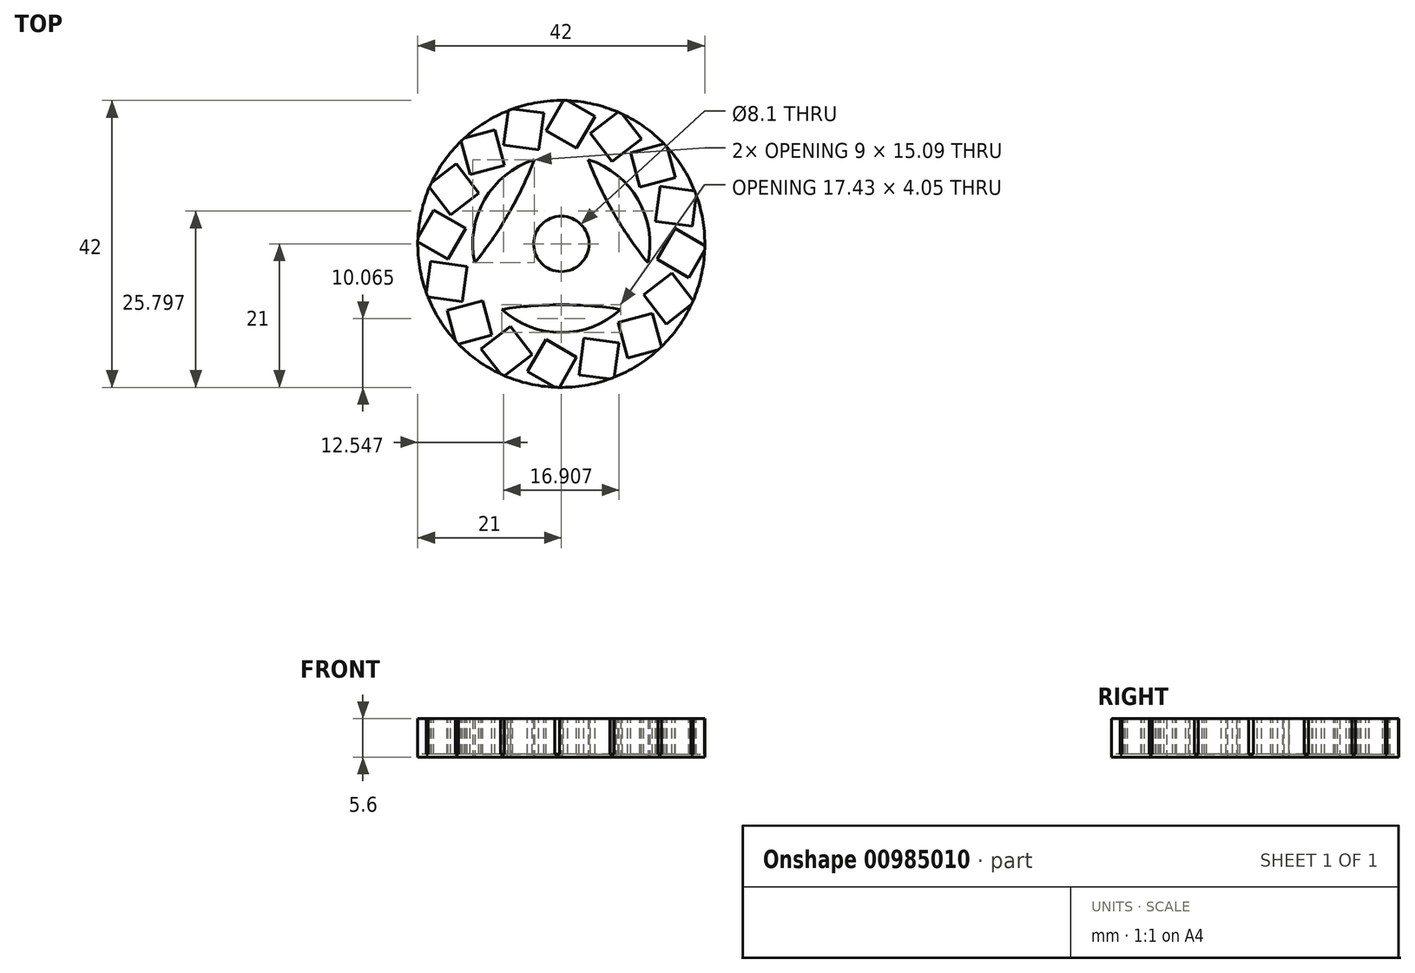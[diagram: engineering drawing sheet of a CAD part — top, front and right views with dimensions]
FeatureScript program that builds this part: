
annotation { "Feature Type Name" : "Feature", "Feature Type Description" : "" }
export const myFeature = defineFeature(function(context is Context, id is Id, definition is map)
    precondition{}
    {
        {
            var Q0;
            Q0=qCreatedBy(makeId("Front.planeOp"),FACE);
            var sketch = newSketch(context, id + "F0", { "sketchPlane" : qUnion([Q0])});
            skLineSegment(sketch, "E0", {"start": v(0, 0) * mm, "end": v(21, 0) * mm});
            skLineSegment(sketch, "E1", {"start": v(21, 0) * mm, "end": v(21, 5.6) * mm});
            skLineSegment(sketch, "E2", {"start": v(21, 5.6) * mm, "end": v(0, 5.6) * mm});
            skLineSegment(sketch, "E3", {"start": v(0, 5.6) * mm, "end": v(0, 0) * mm});
            skSolve(sketch);
        }
        {
            var Q0;
            Q0=qSketchRegion(id+"F0",true);
            var Q1;
            Q1=sQuery(id+"F0.wireOp",EDGE,"E3");
            revolve(context, id + "F1", {"surfaceOperationType" : NewSurfaceOperationType.NEW, "entities" : qUnion([Q0]), "axis" : qUnion([Q1]), "revolveType" : RevolveType.FULL});
        }
        {
            var Q0;
            Q0=qCreatedBy(makeId("Top.planeOp"),FACE);
            var sketch = newSketch(context, id + "F2", { "sketchPlane" : qUnion([Q0])});
            skCircle(sketch, "E4", {"center": v(0, 0) * mm, "radius": 8.9 * mm});
            skCircle(sketch, "E5", {"center": v(0, 0) * mm, "radius": 12.96 * mm});
            skCircle(sketch, "E6", {"center": v(0, 0) * mm, "radius": 17.01 * mm});
            skCircle(sketch, "E7", {"center": v(0, 0) * mm, "radius": 4.05 * mm});
            skCircle(sketch, "E8", {"center": v(0, 12.96) * mm, "radius": 4 * mm});
            skCircle(sketch, "E9.1.0", {"center": v(-11.22, -6.48) * mm, "radius": 4 * mm});
            skCircle(sketch, "E9.2.0", {"center": v(11.22, -6.48) * mm, "radius": 4 * mm});
            skArc(sketch, "E10", {"start": v(-12.67, -2.75) * mm, "mid": v(-7.7, 4.45) * mm, "end": v(-3.95, 12.34) * mm});
            skArc(sketch, "E11", {"start": v(3.95, 12.34) * mm, "mid": v(7.7, 4.44) * mm, "end": v(12.67, -2.75) * mm});
            skArc(sketch, "E12", {"start": v(8.71, -9.6) * mm, "mid": v(0, -8.9) * mm, "end": v(-8.71, -9.6) * mm});
            skLineSegment(sketch, "E13", {"start": v(-3.95, 12.34) * mm, "end": v(-4.58, 16.38) * mm});
            skLineSegment(sketch, "E14", {"start": v(3.95, 12.34) * mm, "end": v(4.58, 16.38) * mm});
            skLineSegment(sketch, "E15.1.0", {"start": v(-8.71, -9.6) * mm, "end": v(-11.9, -12.16) * mm});
            skLineSegment(sketch, "E15.1.1", {"start": v(-12.67, -2.75) * mm, "end": v(-16.48, -4.22) * mm});
            skLineSegment(sketch, "E15.2.0", {"start": v(12.67, -2.75) * mm, "end": v(16.48, -4.22) * mm});
            skLineSegment(sketch, "E15.2.1", {"start": v(8.71, -9.6) * mm, "end": v(11.9, -12.16) * mm});
            skSolve(sketch);
        }
        {
            var Q0;
            Q0=makeQuery(id+"F2.imprint","IMPRINT",FACE,{"disambiguationData":[TD([[makeQuery(id+"F2.imprint","IMPRINT",EDGE,{"derivedFrom":sQuery(id+"F2.wireOp",EDGE,"E7")}),1.0]])]});
            var Q1;
            {var subQ0=sQuery(id+"F2.wireOp",EDGE,"E10");var subQ1=sQuery(id+"F2.wireOp",EDGE,"E4");var subQ2=makeQuery(id+"F2.imprint","INTERSECT",VERTEX,{"disambiguationData":[OD(0.0)],"derivedFrom":[subQ1,subQ0]});Q1=makeQuery(id+"F2.imprint","IMPRINT",FACE,{"disambiguationData":[TD([[makeQuery(id+"F2.imprint","IMPRINT",EDGE,{"disambiguationData":[TD([[subQ2,-1.0]])],"derivedFrom":subQ1}),-1.0]])]});}
            var Q2;
            {var subQ0=sQuery(id+"F2.wireOp",EDGE,"E11");var subQ1=sQuery(id+"F2.wireOp",EDGE,"E4");var subQ2=makeQuery(id+"F2.imprint","INTERSECT",VERTEX,{"disambiguationData":[OD(0.0)],"derivedFrom":[subQ1,subQ0]});Q2=makeQuery(id+"F2.imprint","IMPRINT",FACE,{"disambiguationData":[TD([[makeQuery(id+"F2.imprint","IMPRINT",EDGE,{"disambiguationData":[TD([[subQ2,1.0]])],"derivedFrom":subQ1}),-1.0]])]});}
            var Q3;
            {var subQ0=sQuery(id+"F2.wireOp",EDGE,"E12");var subQ1=sQuery(id+"F2.wireOp",EDGE,"E4");var subQ2=makeQuery(id+"F2.imprint","INTERSECT",VERTEX,{"disambiguationData":[OD(0.0)],"derivedFrom":[subQ1,subQ0]});Q3=makeQuery(id+"F2.imprint","IMPRINT",FACE,{"disambiguationData":[TD([[makeQuery(id+"F2.imprint","IMPRINT",EDGE,{"disambiguationData":[TD([[subQ2,-1.0]])],"derivedFrom":subQ1}),-1.0]])]});}
            extrude(context, id + "F3", {"entities" : qUnion([Q0, Q1, Q2, Q3]), "operationType" : NewBodyOperationType.REMOVE, "depth" : 25 * mm, "offsetDistance" : 25 * mm});
        }
        {
            var Q0;
            Q0=makeQuery(id+"F1.opRevolve","SWEPT_FACE",FACE,{"disambiguationData":[OSD([sQuery(id+"F0.wireOp",EDGE,"E2")])]});
            var sketch = newSketch(context, id + "F4", { "sketchPlane" : qUnion([Q0])});
            skLineSegment(sketch, "E16.bottom", {"start": v(2.25, 14) * mm, "end": v(-2.25, 16.6) * mm});
            skLineSegment(sketch, "E16.top", {"start": v(4.95, 18.68) * mm, "end": v(0.45, 21.28) * mm});
            skLineSegment(sketch, "E16.left", {"start": v(2.25, 14) * mm, "end": v(4.95, 18.68) * mm});
            skLineSegment(sketch, "E16.right", {"start": v(-2.25, 16.6) * mm, "end": v(0.45, 21.28) * mm});
            skLineSegment(sketch, "E17", {"start": v(0, 0) * mm, "end": v(0, 15.3) * mm, "construction": true});
            skLineSegment(sketch, "E18.1.0", {"start": v(-3.28, 13.8) * mm, "end": v(-2.57, 19.15) * mm});
            skLineSegment(sketch, "E18.1.1", {"start": v(-2.57, 19.15) * mm, "end": v(-7.73, 19.83) * mm});
            skLineSegment(sketch, "E18.1.2", {"start": v(-8.43, 14.47) * mm, "end": v(-7.73, 19.83) * mm});
            skLineSegment(sketch, "E18.1.3", {"start": v(-3.28, 13.8) * mm, "end": v(-8.43, 14.47) * mm});
            skLineSegment(sketch, "E18.2.0", {"start": v(-8.3, 11.5) * mm, "end": v(-9.7, 16.7) * mm});
            skLineSegment(sketch, "E18.2.1", {"start": v(-9.7, 16.7) * mm, "end": v(-14.73, 15.36) * mm});
            skLineSegment(sketch, "E18.2.2", {"start": v(-13.33, 10.15) * mm, "end": v(-14.73, 15.36) * mm});
            skLineSegment(sketch, "E18.2.3", {"start": v(-8.3, 11.5) * mm, "end": v(-13.33, 10.15) * mm});
            skLineSegment(sketch, "E18.3.0", {"start": v(-12.07, 7.44) * mm, "end": v(-15.36, 11.72) * mm});
            skLineSegment(sketch, "E18.3.1", {"start": v(-15.36, 11.72) * mm, "end": v(-19.49, 8.56) * mm});
            skLineSegment(sketch, "E18.3.2", {"start": v(-16.2, 4.27) * mm, "end": v(-19.49, 8.56) * mm});
            skLineSegment(sketch, "E18.3.3", {"start": v(-12.07, 7.44) * mm, "end": v(-16.2, 4.27) * mm});
            skLineSegment(sketch, "E18.4.0", {"start": v(-14, 2.25) * mm, "end": v(-18.68, 4.95) * mm});
            skLineSegment(sketch, "E18.4.1", {"start": v(-18.68, 4.95) * mm, "end": v(-21.28, 0.45) * mm});
            skLineSegment(sketch, "E18.4.2", {"start": v(-16.6, -2.25) * mm, "end": v(-21.28, 0.45) * mm});
            skLineSegment(sketch, "E18.4.3", {"start": v(-14, 2.25) * mm, "end": v(-16.6, -2.25) * mm});
            skLineSegment(sketch, "E18.5.0", {"start": v(-13.8, -3.28) * mm, "end": v(-19.15, -2.57) * mm});
            skLineSegment(sketch, "E18.5.1", {"start": v(-19.15, -2.57) * mm, "end": v(-19.83, -7.73) * mm});
            skLineSegment(sketch, "E18.5.2", {"start": v(-14.47, -8.43) * mm, "end": v(-19.83, -7.73) * mm});
            skLineSegment(sketch, "E18.5.3", {"start": v(-13.8, -3.28) * mm, "end": v(-14.47, -8.43) * mm});
            skLineSegment(sketch, "E18.6.0", {"start": v(-11.5, -8.3) * mm, "end": v(-16.7, -9.7) * mm});
            skLineSegment(sketch, "E18.6.1", {"start": v(-16.7, -9.7) * mm, "end": v(-15.36, -14.73) * mm});
            skLineSegment(sketch, "E18.6.2", {"start": v(-10.15, -13.33) * mm, "end": v(-15.36, -14.73) * mm});
            skLineSegment(sketch, "E18.6.3", {"start": v(-11.5, -8.3) * mm, "end": v(-10.15, -13.33) * mm});
            skLineSegment(sketch, "E18.7.0", {"start": v(-7.44, -12.07) * mm, "end": v(-11.72, -15.36) * mm});
            skLineSegment(sketch, "E18.7.1", {"start": v(-11.72, -15.36) * mm, "end": v(-8.56, -19.49) * mm});
            skLineSegment(sketch, "E18.7.2", {"start": v(-4.27, -16.2) * mm, "end": v(-8.56, -19.49) * mm});
            skLineSegment(sketch, "E18.7.3", {"start": v(-7.44, -12.07) * mm, "end": v(-4.27, -16.2) * mm});
            skLineSegment(sketch, "E18.8.0", {"start": v(-2.25, -14) * mm, "end": v(-4.95, -18.68) * mm});
            skLineSegment(sketch, "E18.8.1", {"start": v(-4.95, -18.68) * mm, "end": v(-0.45, -21.28) * mm});
            skLineSegment(sketch, "E18.8.2", {"start": v(2.25, -16.6) * mm, "end": v(-0.45, -21.28) * mm});
            skLineSegment(sketch, "E18.8.3", {"start": v(-2.25, -14) * mm, "end": v(2.25, -16.6) * mm});
            skLineSegment(sketch, "E18.9.0", {"start": v(3.28, -13.8) * mm, "end": v(2.57, -19.15) * mm});
            skLineSegment(sketch, "E18.9.1", {"start": v(2.57, -19.15) * mm, "end": v(7.73, -19.83) * mm});
            skLineSegment(sketch, "E18.9.2", {"start": v(8.43, -14.47) * mm, "end": v(7.73, -19.83) * mm});
            skLineSegment(sketch, "E18.9.3", {"start": v(3.28, -13.8) * mm, "end": v(8.43, -14.47) * mm});
            skLineSegment(sketch, "E18.10.0", {"start": v(8.3, -11.5) * mm, "end": v(9.7, -16.7) * mm});
            skLineSegment(sketch, "E18.10.1", {"start": v(9.7, -16.7) * mm, "end": v(14.73, -15.36) * mm});
            skLineSegment(sketch, "E18.10.2", {"start": v(13.33, -10.15) * mm, "end": v(14.73, -15.36) * mm});
            skLineSegment(sketch, "E18.10.3", {"start": v(8.3, -11.5) * mm, "end": v(13.33, -10.15) * mm});
            skLineSegment(sketch, "E18.11.0", {"start": v(12.07, -7.44) * mm, "end": v(15.36, -11.72) * mm});
            skLineSegment(sketch, "E18.11.1", {"start": v(15.36, -11.72) * mm, "end": v(19.49, -8.56) * mm});
            skLineSegment(sketch, "E18.11.2", {"start": v(16.2, -4.27) * mm, "end": v(19.49, -8.56) * mm});
            skLineSegment(sketch, "E18.11.3", {"start": v(12.07, -7.44) * mm, "end": v(16.2, -4.27) * mm});
            skLineSegment(sketch, "E18.12.0", {"start": v(14, -2.25) * mm, "end": v(18.68, -4.95) * mm});
            skLineSegment(sketch, "E18.12.1", {"start": v(18.68, -4.95) * mm, "end": v(21.28, -0.45) * mm});
            skLineSegment(sketch, "E18.12.2", {"start": v(16.6, 2.25) * mm, "end": v(21.28, -0.45) * mm});
            skLineSegment(sketch, "E18.12.3", {"start": v(14, -2.25) * mm, "end": v(16.6, 2.25) * mm});
            skLineSegment(sketch, "E18.13.0", {"start": v(13.8, 3.28) * mm, "end": v(19.15, 2.57) * mm});
            skLineSegment(sketch, "E18.13.1", {"start": v(19.15, 2.57) * mm, "end": v(19.83, 7.73) * mm});
            skLineSegment(sketch, "E18.13.2", {"start": v(14.47, 8.43) * mm, "end": v(19.83, 7.73) * mm});
            skLineSegment(sketch, "E18.13.3", {"start": v(13.8, 3.28) * mm, "end": v(14.47, 8.43) * mm});
            skLineSegment(sketch, "E18.14.0", {"start": v(11.5, 8.3) * mm, "end": v(16.7, 9.7) * mm});
            skLineSegment(sketch, "E18.14.1", {"start": v(16.7, 9.7) * mm, "end": v(15.36, 14.73) * mm});
            skLineSegment(sketch, "E18.14.2", {"start": v(10.15, 13.33) * mm, "end": v(15.36, 14.73) * mm});
            skLineSegment(sketch, "E18.14.3", {"start": v(11.5, 8.3) * mm, "end": v(10.15, 13.33) * mm});
            skLineSegment(sketch, "E18.15.0", {"start": v(7.44, 12.07) * mm, "end": v(11.72, 15.36) * mm});
            skLineSegment(sketch, "E18.15.1", {"start": v(11.72, 15.36) * mm, "end": v(8.56, 19.49) * mm});
            skLineSegment(sketch, "E18.15.2", {"start": v(4.27, 16.2) * mm, "end": v(8.56, 19.49) * mm});
            skLineSegment(sketch, "E18.15.3", {"start": v(7.44, 12.07) * mm, "end": v(4.27, 16.2) * mm});
            skPoint(sketch, "E18.center", {"position": v(0, 0) * mm});
            skLineSegment(sketch, "E19", {"start": v(0, 0) * mm, "end": v(0, 21) * mm});
            skLineSegment(sketch, "E20.1.0", {"start": v(0, 0) * mm, "end": v(-18.19, -10.5) * mm});
            skLineSegment(sketch, "E20.2.0", {"start": v(0, 0) * mm, "end": v(18.19, -10.5) * mm});
            skLineSegment(sketch, "E21", {"start": v(0, 15.3) * mm, "end": v(0, 15.7) * mm});
            skSolve(sketch);
        }
        {
            var Q0;
            {var subQ0=sQuery(id+"F4.wireOp",EDGE,"6b0e4d02-cffa-4799-8ca5-8f1609af44a9.1.3");Q0=makeQuery(id+"F4.imprint","IMPRINT",FACE,{"disambiguationData":[TD([[makeQuery(id+"F4.imprint","IMPRINT",EDGE,{"derivedFrom":subQ0}),-1.0]])]});}
            var Q1;
            {var subQ0=sQuery(id+"F4.wireOp",EDGE,"E16.bottom");Q1=makeQuery(id+"F4.imprint","IMPRINT",FACE,{"disambiguationData":[TD([[makeQuery(id+"F4.imprint","IMPRINT",EDGE,{"derivedFrom":subQ0}),-1.0]])]});}
            var Q2;
            {var subQ0=sQuery(id+"F4.wireOp",EDGE,"90cd43ab-74c5-4661-9c80-5ee8405ae9ff.9.15.0");Q2=makeQuery(id+"F4.imprint","IMPRINT",FACE,{"disambiguationData":[TD([[makeQuery(id+"F4.imprint","IMPRINT",EDGE,{"derivedFrom":subQ0}),-1.0]])]});}
            var Q3;
            {var subQ0=sQuery(id+"F4.wireOp",EDGE,"90cd43ab-74c5-4661-9c80-5ee8405ae9ff.9.14.0");Q3=makeQuery(id+"F4.imprint","IMPRINT",FACE,{"disambiguationData":[TD([[makeQuery(id+"F4.imprint","IMPRINT",EDGE,{"derivedFrom":subQ0}),-1.0]])]});}
            var Q4;
            {var subQ0=sQuery(id+"F4.wireOp",EDGE,"90cd43ab-74c5-4661-9c80-5ee8405ae9ff.9.13.0");Q4=makeQuery(id+"F4.imprint","IMPRINT",FACE,{"disambiguationData":[TD([[makeQuery(id+"F4.imprint","IMPRINT",EDGE,{"derivedFrom":subQ0}),-1.0]])]});}
            var Q5;
            {var subQ0=sQuery(id+"F4.wireOp",EDGE,"90cd43ab-74c5-4661-9c80-5ee8405ae9ff.9.12.0");Q5=makeQuery(id+"F4.imprint","IMPRINT",FACE,{"disambiguationData":[TD([[makeQuery(id+"F4.imprint","IMPRINT",EDGE,{"derivedFrom":subQ0}),-1.0]])]});}
            var Q6;
            {var subQ0=sQuery(id+"F4.wireOp",EDGE,"90cd43ab-74c5-4661-9c80-5ee8405ae9ff.9.11.0");Q6=makeQuery(id+"F4.imprint","IMPRINT",FACE,{"disambiguationData":[TD([[makeQuery(id+"F4.imprint","IMPRINT",EDGE,{"derivedFrom":subQ0}),-1.0]])]});}
            var Q7;
            {var subQ0=sQuery(id+"F4.wireOp",EDGE,"90cd43ab-74c5-4661-9c80-5ee8405ae9ff.9.10.0");Q7=makeQuery(id+"F4.imprint","IMPRINT",FACE,{"disambiguationData":[TD([[makeQuery(id+"F4.imprint","IMPRINT",EDGE,{"derivedFrom":subQ0}),-1.0]])]});}
            var Q8;
            {var subQ0=sQuery(id+"F4.wireOp",EDGE,"90cd43ab-74c5-4661-9c80-5ee8405ae9ff.9.9.0");Q8=makeQuery(id+"F4.imprint","IMPRINT",FACE,{"disambiguationData":[TD([[makeQuery(id+"F4.imprint","IMPRINT",EDGE,{"derivedFrom":subQ0}),-1.0]])]});}
            var Q9;
            {var subQ0=sQuery(id+"F4.wireOp",EDGE,"90cd43ab-74c5-4661-9c80-5ee8405ae9ff.9.8.0");Q9=makeQuery(id+"F4.imprint","IMPRINT",FACE,{"disambiguationData":[TD([[makeQuery(id+"F4.imprint","IMPRINT",EDGE,{"derivedFrom":subQ0}),-1.0]])]});}
            var Q10;
            {var subQ0=sQuery(id+"F4.wireOp",EDGE,"90cd43ab-74c5-4661-9c80-5ee8405ae9ff.9.7.0");Q10=makeQuery(id+"F4.imprint","IMPRINT",FACE,{"disambiguationData":[TD([[makeQuery(id+"F4.imprint","IMPRINT",EDGE,{"derivedFrom":subQ0}),-1.0]])]});}
            var Q11;
            {var subQ0=sQuery(id+"F4.wireOp",EDGE,"90cd43ab-74c5-4661-9c80-5ee8405ae9ff.9.6.0");Q11=makeQuery(id+"F4.imprint","IMPRINT",FACE,{"disambiguationData":[TD([[makeQuery(id+"F4.imprint","IMPRINT",EDGE,{"derivedFrom":subQ0}),-1.0]])]});}
            var Q12;
            {var subQ0=sQuery(id+"F4.wireOp",EDGE,"90cd43ab-74c5-4661-9c80-5ee8405ae9ff.9.5.0");Q12=makeQuery(id+"F4.imprint","IMPRINT",FACE,{"disambiguationData":[TD([[makeQuery(id+"F4.imprint","IMPRINT",EDGE,{"derivedFrom":subQ0}),-1.0]])]});}
            var Q13;
            {var subQ0=sQuery(id+"F4.wireOp",EDGE,"90cd43ab-74c5-4661-9c80-5ee8405ae9ff.9.4.0");Q13=makeQuery(id+"F4.imprint","IMPRINT",FACE,{"disambiguationData":[TD([[makeQuery(id+"F4.imprint","IMPRINT",EDGE,{"derivedFrom":subQ0}),-1.0]])]});}
            var Q14;
            {var subQ0=sQuery(id+"F4.wireOp",EDGE,"90cd43ab-74c5-4661-9c80-5ee8405ae9ff.9.3.0");Q14=makeQuery(id+"F4.imprint","IMPRINT",FACE,{"disambiguationData":[TD([[makeQuery(id+"F4.imprint","IMPRINT",EDGE,{"derivedFrom":subQ0}),-1.0]])]});}
            var Q15;
            {var subQ0=sQuery(id+"F4.wireOp",EDGE,"6b0e4d02-cffa-4799-8ca5-8f1609af44a9.2.3");Q15=makeQuery(id+"F4.imprint","IMPRINT",FACE,{"disambiguationData":[TD([[makeQuery(id+"F4.imprint","IMPRINT",EDGE,{"derivedFrom":subQ0}),-1.0]])]});}
            var Q16;
            Q16=makeQuery(id+"F4.imprint","IMPRINT",FACE,{"disambiguationData":[TD([[makeQuery(id+"F4.imprint","IMPRINT",EDGE,{"derivedFrom":sQuery(id+"F4.wireOp",EDGE,"d7aad85c-847f-47a7-b33a-bcce6dfe605d.15.0")}),-1.0]])]});
            var Q17;
            Q17=makeQuery(id+"F4.imprint","IMPRINT",FACE,{"disambiguationData":[TD([[makeQuery(id+"F4.imprint","IMPRINT",EDGE,{"derivedFrom":sQuery(id+"F4.wireOp",EDGE,"d7aad85c-847f-47a7-b33a-bcce6dfe605d.14.0")}),-1.0]])]});
            var Q18;
            Q18=makeQuery(id+"F4.imprint","IMPRINT",FACE,{"disambiguationData":[TD([[makeQuery(id+"F4.imprint","IMPRINT",EDGE,{"derivedFrom":sQuery(id+"F4.wireOp",EDGE,"d7aad85c-847f-47a7-b33a-bcce6dfe605d.13.0")}),-1.0]])]});
            var Q19;
            Q19=makeQuery(id+"F4.imprint","IMPRINT",FACE,{"disambiguationData":[TD([[makeQuery(id+"F4.imprint","IMPRINT",EDGE,{"derivedFrom":sQuery(id+"F4.wireOp",EDGE,"d7aad85c-847f-47a7-b33a-bcce6dfe605d.12.0")}),-1.0]])]});
            var Q20;
            Q20=makeQuery(id+"F4.imprint","IMPRINT",FACE,{"disambiguationData":[TD([[makeQuery(id+"F4.imprint","IMPRINT",EDGE,{"derivedFrom":sQuery(id+"F4.wireOp",EDGE,"d7aad85c-847f-47a7-b33a-bcce6dfe605d.11.0")}),-1.0]])]});
            var Q21;
            Q21=makeQuery(id+"F4.imprint","IMPRINT",FACE,{"disambiguationData":[TD([[makeQuery(id+"F4.imprint","IMPRINT",EDGE,{"derivedFrom":sQuery(id+"F4.wireOp",EDGE,"d7aad85c-847f-47a7-b33a-bcce6dfe605d.10.0")}),-1.0]])]});
            var Q22;
            Q22=makeQuery(id+"F4.imprint","IMPRINT",FACE,{"disambiguationData":[TD([[makeQuery(id+"F4.imprint","IMPRINT",EDGE,{"derivedFrom":sQuery(id+"F4.wireOp",EDGE,"d7aad85c-847f-47a7-b33a-bcce6dfe605d.9.0")}),-1.0]])]});
            var Q23;
            Q23=makeQuery(id+"F4.imprint","IMPRINT",FACE,{"disambiguationData":[TD([[makeQuery(id+"F4.imprint","IMPRINT",EDGE,{"derivedFrom":sQuery(id+"F4.wireOp",EDGE,"d7aad85c-847f-47a7-b33a-bcce6dfe605d.8.0")}),-1.0]])]});
            var Q24;
            Q24=makeQuery(id+"F4.imprint","IMPRINT",FACE,{"disambiguationData":[TD([[makeQuery(id+"F4.imprint","IMPRINT",EDGE,{"derivedFrom":sQuery(id+"F4.wireOp",EDGE,"d7aad85c-847f-47a7-b33a-bcce6dfe605d.7.0")}),-1.0]])]});
            var Q25;
            Q25=makeQuery(id+"F4.imprint","IMPRINT",FACE,{"disambiguationData":[TD([[makeQuery(id+"F4.imprint","IMPRINT",EDGE,{"derivedFrom":sQuery(id+"F4.wireOp",EDGE,"d7aad85c-847f-47a7-b33a-bcce6dfe605d.6.0")}),-1.0]])]});
            var Q26;
            Q26=makeQuery(id+"F4.imprint","IMPRINT",FACE,{"disambiguationData":[TD([[makeQuery(id+"F4.imprint","IMPRINT",EDGE,{"derivedFrom":sQuery(id+"F4.wireOp",EDGE,"d7aad85c-847f-47a7-b33a-bcce6dfe605d.5.0")}),-1.0]])]});
            var Q27;
            Q27=makeQuery(id+"F4.imprint","IMPRINT",FACE,{"disambiguationData":[TD([[makeQuery(id+"F4.imprint","IMPRINT",EDGE,{"derivedFrom":sQuery(id+"F4.wireOp",EDGE,"d7aad85c-847f-47a7-b33a-bcce6dfe605d.4.0")}),-1.0]])]});
            var Q28;
            Q28=makeQuery(id+"F4.imprint","IMPRINT",FACE,{"disambiguationData":[TD([[makeQuery(id+"F4.imprint","IMPRINT",EDGE,{"derivedFrom":sQuery(id+"F4.wireOp",EDGE,"d7aad85c-847f-47a7-b33a-bcce6dfe605d.3.0")}),-1.0]])]});
            var Q29;
            Q29=makeQuery(id+"F4.imprint","IMPRINT",FACE,{"disambiguationData":[TD([[makeQuery(id+"F4.imprint","IMPRINT",EDGE,{"derivedFrom":sQuery(id+"F4.wireOp",EDGE,"d7aad85c-847f-47a7-b33a-bcce6dfe605d.2.0")}),-1.0]])]});
            var Q30;
            Q30=makeQuery(id+"F4.imprint","IMPRINT",FACE,{"disambiguationData":[TD([[makeQuery(id+"F4.imprint","IMPRINT",EDGE,{"derivedFrom":sQuery(id+"F4.wireOp",EDGE,"d7aad85c-847f-47a7-b33a-bcce6dfe605d.1.0")}),-1.0]])]});
            var Q31;
            Q31=makeQuery(id+"F4.imprint","IMPRINT",FACE,{"disambiguationData":[TD([[makeQuery(id+"F4.imprint","IMPRINT",EDGE,{"derivedFrom":sQuery(id+"F4.wireOp",EDGE,"E18.15.0")}),1.0]])]});
            var Q32;
            Q32=makeQuery(id+"F4.imprint","IMPRINT",FACE,{"disambiguationData":[TD([[makeQuery(id+"F4.imprint","IMPRINT",EDGE,{"derivedFrom":sQuery(id+"F4.wireOp",EDGE,"E18.14.0")}),1.0]])]});
            var Q33;
            Q33=makeQuery(id+"F4.imprint","IMPRINT",FACE,{"disambiguationData":[TD([[makeQuery(id+"F4.imprint","IMPRINT",EDGE,{"derivedFrom":sQuery(id+"F4.wireOp",EDGE,"E18.13.0")}),1.0]])]});
            var Q34;
            Q34=makeQuery(id+"F4.imprint","IMPRINT",FACE,{"disambiguationData":[TD([[makeQuery(id+"F4.imprint","IMPRINT",EDGE,{"derivedFrom":sQuery(id+"F4.wireOp",EDGE,"E18.12.0")}),1.0]])]});
            var Q35;
            Q35=makeQuery(id+"F4.imprint","IMPRINT",FACE,{"disambiguationData":[TD([[makeQuery(id+"F4.imprint","IMPRINT",EDGE,{"derivedFrom":sQuery(id+"F4.wireOp",EDGE,"E18.11.0")}),1.0]])]});
            var Q36;
            Q36=makeQuery(id+"F4.imprint","IMPRINT",FACE,{"disambiguationData":[TD([[makeQuery(id+"F4.imprint","IMPRINT",EDGE,{"derivedFrom":sQuery(id+"F4.wireOp",EDGE,"E18.10.0")}),1.0]])]});
            var Q37;
            Q37=makeQuery(id+"F4.imprint","IMPRINT",FACE,{"disambiguationData":[TD([[makeQuery(id+"F4.imprint","IMPRINT",EDGE,{"derivedFrom":sQuery(id+"F4.wireOp",EDGE,"E18.9.0")}),1.0]])]});
            var Q38;
            Q38=makeQuery(id+"F4.imprint","IMPRINT",FACE,{"disambiguationData":[TD([[makeQuery(id+"F4.imprint","IMPRINT",EDGE,{"derivedFrom":sQuery(id+"F4.wireOp",EDGE,"E18.8.0")}),1.0]])]});
            var Q39;
            Q39=makeQuery(id+"F4.imprint","IMPRINT",FACE,{"disambiguationData":[TD([[makeQuery(id+"F4.imprint","IMPRINT",EDGE,{"derivedFrom":sQuery(id+"F4.wireOp",EDGE,"E18.7.0")}),1.0]])]});
            var Q40;
            Q40=makeQuery(id+"F4.imprint","IMPRINT",FACE,{"disambiguationData":[TD([[makeQuery(id+"F4.imprint","IMPRINT",EDGE,{"derivedFrom":sQuery(id+"F4.wireOp",EDGE,"E18.6.0")}),1.0]])]});
            var Q41;
            Q41=makeQuery(id+"F4.imprint","IMPRINT",FACE,{"disambiguationData":[TD([[makeQuery(id+"F4.imprint","IMPRINT",EDGE,{"derivedFrom":sQuery(id+"F4.wireOp",EDGE,"E18.4.0")}),1.0]])]});
            var Q42;
            Q42=makeQuery(id+"F4.imprint","IMPRINT",FACE,{"disambiguationData":[TD([[makeQuery(id+"F4.imprint","IMPRINT",EDGE,{"derivedFrom":sQuery(id+"F4.wireOp",EDGE,"E18.3.0")}),1.0]])]});
            var Q43;
            Q43=makeQuery(id+"F4.imprint","IMPRINT",FACE,{"disambiguationData":[TD([[makeQuery(id+"F4.imprint","IMPRINT",EDGE,{"derivedFrom":sQuery(id+"F4.wireOp",EDGE,"E18.2.0")}),1.0]])]});
            var Q44;
            Q44=makeQuery(id+"F4.imprint","IMPRINT",FACE,{"disambiguationData":[TD([[makeQuery(id+"F4.imprint","IMPRINT",EDGE,{"derivedFrom":sQuery(id+"F4.wireOp",EDGE,"E18.1.0")}),1.0]])]});
            var Q45;
            {var subQ0=sQuery(id+"F4.wireOp",EDGE,"E18.5.0");var subQ1=sQuery(id+"F2.wireOp",EDGE,"E15.1.1");var subQ2=makeQuery(id+"F1.opRevolve","SWEPT_FACE",FACE,{"disambiguationData":[OSD([sQuery(id+"F0.wireOp",EDGE,"E2")])]});var subQ3=makeQuery(id+"F3.boolean.opBoolean","INTERSECT",EDGE,{"derivedFrom":[subQ2,makeQuery(id+"F3.opExtrude","SWEPT_FACE",FACE,{"disambiguationData":[OSD([subQ1])]})]});var subQ4=makeQuery(id+"F4.imprint","INTERSECT",VERTEX,{"derivedFrom":[subQ3,subQ0]});Q45=makeQuery(id+"F4.imprint","IMPRINT",FACE,{"disambiguationData":[TD([[makeQuery(id+"F4.imprint","IMPRINT",EDGE,{"disambiguationData":[TD([[subQ4,-1.0]])],"derivedFrom":subQ0}),1.0]])]});}
            var Q46;
            {var subQ0=sQuery(id+"F4.wireOp",EDGE,"E18.1.3");var subQ1=sQuery(id+"F4.wireOp",EDGE,"E18.1.2");var subQ2=makeQuery(id+"F4.imprint","INTERSECT",VERTEX,{"derivedFrom":[subQ1,subQ0]});Q46=makeQuery(id+"F4.imprint","IMPRINT",FACE,{"disambiguationData":[TD([[makeQuery(id+"F4.imprint","IMPRINT",EDGE,{"disambiguationData":[TD([[subQ2,1.0]])],"derivedFrom":subQ0}),-1.0]])]});}
            var Q47;
            {var subQ13=sQuery(id+"F4.wireOp",EDGE,"E18.5.3");Q47=makeQuery(id+"F4.imprint","IMPRINT",FACE,{"disambiguationData":[TD([[makeQuery(id+"F4.imprint","IMPRINT",EDGE,{"derivedFrom":subQ13}),-1.0]])]});}
            var Q48;
            {var subQ0=sQuery(id+"F4.wireOp",EDGE,"E18.4.1");var subQ9=sQuery(id+"F4.wireOp",EDGE,"E18.4.0");var subQ10=makeQuery(id+"F4.imprint","INTERSECT",VERTEX,{"derivedFrom":[subQ9,subQ0]});Q48=makeQuery(id+"F4.imprint","IMPRINT",FACE,{"disambiguationData":[TD([[makeQuery(id+"F4.imprint","IMPRINT",EDGE,{"disambiguationData":[TD([[subQ10,-1.0]])],"derivedFrom":subQ0}),1.0]])]});}
            var Q49;
            {var subQ9=sQuery(id+"F4.wireOp",EDGE,"E18.6.3");var subQ10=sQuery(id+"F4.wireOp",EDGE,"E18.6.0");var subQ11=makeQuery(id+"F4.imprint","INTERSECT",VERTEX,{"derivedFrom":[subQ10,subQ9]});Q49=makeQuery(id+"F4.imprint","IMPRINT",FACE,{"disambiguationData":[TD([[makeQuery(id+"F4.imprint","IMPRINT",EDGE,{"disambiguationData":[TD([[subQ11,-1.0]])],"derivedFrom":subQ10}),1.0]])]});}
            var Q50;
            {var subQ7=sQuery(id+"F4.wireOp",EDGE,"E18.3.1");var subQ9=sQuery(id+"F4.wireOp",EDGE,"E18.3.0");var subQ10=makeQuery(id+"F4.imprint","INTERSECT",VERTEX,{"derivedFrom":[subQ9,subQ7]});Q50=makeQuery(id+"F4.imprint","IMPRINT",FACE,{"disambiguationData":[TD([[makeQuery(id+"F4.imprint","IMPRINT",EDGE,{"disambiguationData":[TD([[subQ10,-1.0]])],"derivedFrom":subQ7}),1.0]])]});}
            var Q51;
            {var subQ0=sQuery(id+"F4.wireOp",EDGE,"E18.2.1");var subQ9=sQuery(id+"F4.wireOp",EDGE,"E18.2.0");var subQ11=makeQuery(id+"F4.imprint","INTERSECT",VERTEX,{"derivedFrom":[subQ9,subQ0]});Q51=makeQuery(id+"F4.imprint","IMPRINT",FACE,{"disambiguationData":[TD([[makeQuery(id+"F4.imprint","IMPRINT",EDGE,{"disambiguationData":[TD([[subQ11,-1.0]])],"derivedFrom":subQ0}),1.0]])]});}
            var Q52;
            {var subQ5=sQuery(id+"F4.wireOp",EDGE,"E16.left");Q52=makeQuery(id+"F4.imprint","IMPRINT",FACE,{"disambiguationData":[TD([[makeQuery(id+"F4.imprint","IMPRINT",EDGE,{"derivedFrom":subQ5}),1.0]])]});}
            var Q53;
            {var subQ6=sQuery(id+"F4.wireOp",EDGE,"E18.15.1");var subQ12=sQuery(id+"F4.wireOp",EDGE,"E18.15.0");var subQ13=makeQuery(id+"F4.imprint","INTERSECT",VERTEX,{"derivedFrom":[subQ12,subQ6]});Q53=makeQuery(id+"F4.imprint","IMPRINT",FACE,{"disambiguationData":[TD([[makeQuery(id+"F4.imprint","IMPRINT",EDGE,{"disambiguationData":[TD([[subQ13,-1.0]])],"derivedFrom":subQ6}),1.0]])]});}
            var Q54;
            {var subQ0=sQuery(id+"F4.wireOp",EDGE,"E18.14.1");var subQ9=sQuery(id+"F4.wireOp",EDGE,"E18.14.0");var subQ10=makeQuery(id+"F4.imprint","INTERSECT",VERTEX,{"derivedFrom":[subQ9,subQ0]});Q54=makeQuery(id+"F4.imprint","IMPRINT",FACE,{"disambiguationData":[TD([[makeQuery(id+"F4.imprint","IMPRINT",EDGE,{"disambiguationData":[TD([[subQ10,-1.0]])],"derivedFrom":subQ0}),1.0]])]});}
            var Q55;
            {var subQ0=sQuery(id+"F4.wireOp",EDGE,"E18.13.1");var subQ6=sQuery(id+"F4.wireOp",EDGE,"E18.13.0");var subQ11=makeQuery(id+"F4.imprint","INTERSECT",VERTEX,{"derivedFrom":[subQ6,subQ0]});Q55=makeQuery(id+"F4.imprint","IMPRINT",FACE,{"disambiguationData":[TD([[makeQuery(id+"F4.imprint","IMPRINT",EDGE,{"disambiguationData":[TD([[subQ11,-1.0]])],"derivedFrom":subQ0}),1.0]])]});}
            var Q56;
            {var subQ7=sQuery(id+"F4.wireOp",EDGE,"E18.12.1");var subQ9=sQuery(id+"F4.wireOp",EDGE,"E18.12.0");var subQ10=makeQuery(id+"F4.imprint","INTERSECT",VERTEX,{"derivedFrom":[subQ9,subQ7]});Q56=makeQuery(id+"F4.imprint","IMPRINT",FACE,{"disambiguationData":[TD([[makeQuery(id+"F4.imprint","IMPRINT",EDGE,{"disambiguationData":[TD([[subQ10,-1.0]])],"derivedFrom":subQ7}),1.0]])]});}
            var Q57;
            {var subQ3=sQuery(id+"F4.wireOp",EDGE,"E18.11.3");var subQ5=sQuery(id+"F4.wireOp",EDGE,"E18.11.2");var subQ6=makeQuery(id+"F4.imprint","INTERSECT",VERTEX,{"derivedFrom":[subQ5,subQ3]});Q57=makeQuery(id+"F4.imprint","IMPRINT",FACE,{"disambiguationData":[TD([[makeQuery(id+"F4.imprint","IMPRINT",EDGE,{"disambiguationData":[TD([[subQ6,1.0]])],"derivedFrom":subQ3}),-1.0]])]});}
            var Q58;
            {var subQ13=sQuery(id+"F4.wireOp",EDGE,"E18.10.0");var subQ15=sQuery(id+"F4.wireOp",EDGE,"E18.10.1");var subQ16=makeQuery(id+"F4.imprint","INTERSECT",VERTEX,{"derivedFrom":[subQ13,subQ15]});Q58=makeQuery(id+"F4.imprint","IMPRINT",FACE,{"disambiguationData":[TD([[makeQuery(id+"F4.imprint","IMPRINT",EDGE,{"disambiguationData":[TD([[subQ16,-1.0]])],"derivedFrom":subQ15}),1.0]])]});}
            var Q59;
            {var subQ0=sQuery(id+"F4.wireOp",EDGE,"E18.9.1");var subQ6=sQuery(id+"F4.wireOp",EDGE,"E18.9.0");var subQ7=makeQuery(id+"F4.imprint","INTERSECT",VERTEX,{"derivedFrom":[subQ6,subQ0]});Q59=makeQuery(id+"F4.imprint","IMPRINT",FACE,{"disambiguationData":[TD([[makeQuery(id+"F4.imprint","IMPRINT",EDGE,{"disambiguationData":[TD([[subQ7,-1.0]])],"derivedFrom":subQ0}),1.0]])]});}
            var Q60;
            {var subQ0=sQuery(id+"F4.wireOp",EDGE,"E18.8.1");var subQ9=sQuery(id+"F4.wireOp",EDGE,"E18.8.0");var subQ10=makeQuery(id+"F4.imprint","INTERSECT",VERTEX,{"derivedFrom":[subQ9,subQ0]});Q60=makeQuery(id+"F4.imprint","IMPRINT",FACE,{"disambiguationData":[TD([[makeQuery(id+"F4.imprint","IMPRINT",EDGE,{"disambiguationData":[TD([[subQ10,-1.0]])],"derivedFrom":subQ0}),1.0]])]});}
            var Q61;
            {var subQ7=sQuery(id+"F4.wireOp",EDGE,"E18.7.1");var subQ9=sQuery(id+"F4.wireOp",EDGE,"E18.7.0");var subQ10=makeQuery(id+"F4.imprint","INTERSECT",VERTEX,{"derivedFrom":[subQ9,subQ7]});Q61=makeQuery(id+"F4.imprint","IMPRINT",FACE,{"disambiguationData":[TD([[makeQuery(id+"F4.imprint","IMPRINT",EDGE,{"disambiguationData":[TD([[subQ10,-1.0]])],"derivedFrom":subQ7}),1.0]])]});}
            extrude(context, id + "F5", {"entities" : qUnion([Q0, Q1, Q2, Q3, Q4, Q5, Q6, Q7, Q8, Q9, Q10, Q11, Q12, Q13, Q14, Q15, Q16, Q17, Q18, Q19, Q20, Q21, Q22, Q23, Q24, Q25, Q26, Q27, Q28, Q29, Q30, Q31, Q32, Q33, Q34, Q35, Q36, Q37, Q38, Q39, Q40, Q41, Q42, Q43, Q44, Q45, Q46, Q47, Q48, Q49, Q50, Q51, Q52, Q53, Q54, Q55, Q56, Q57, Q58, Q59, Q60, Q61]), "operationType" : NewBodyOperationType.REMOVE, "oppositeDirection" : true, "depth" : 5.2 * mm, "offsetDistance" : 25 * mm});
        }
    });
